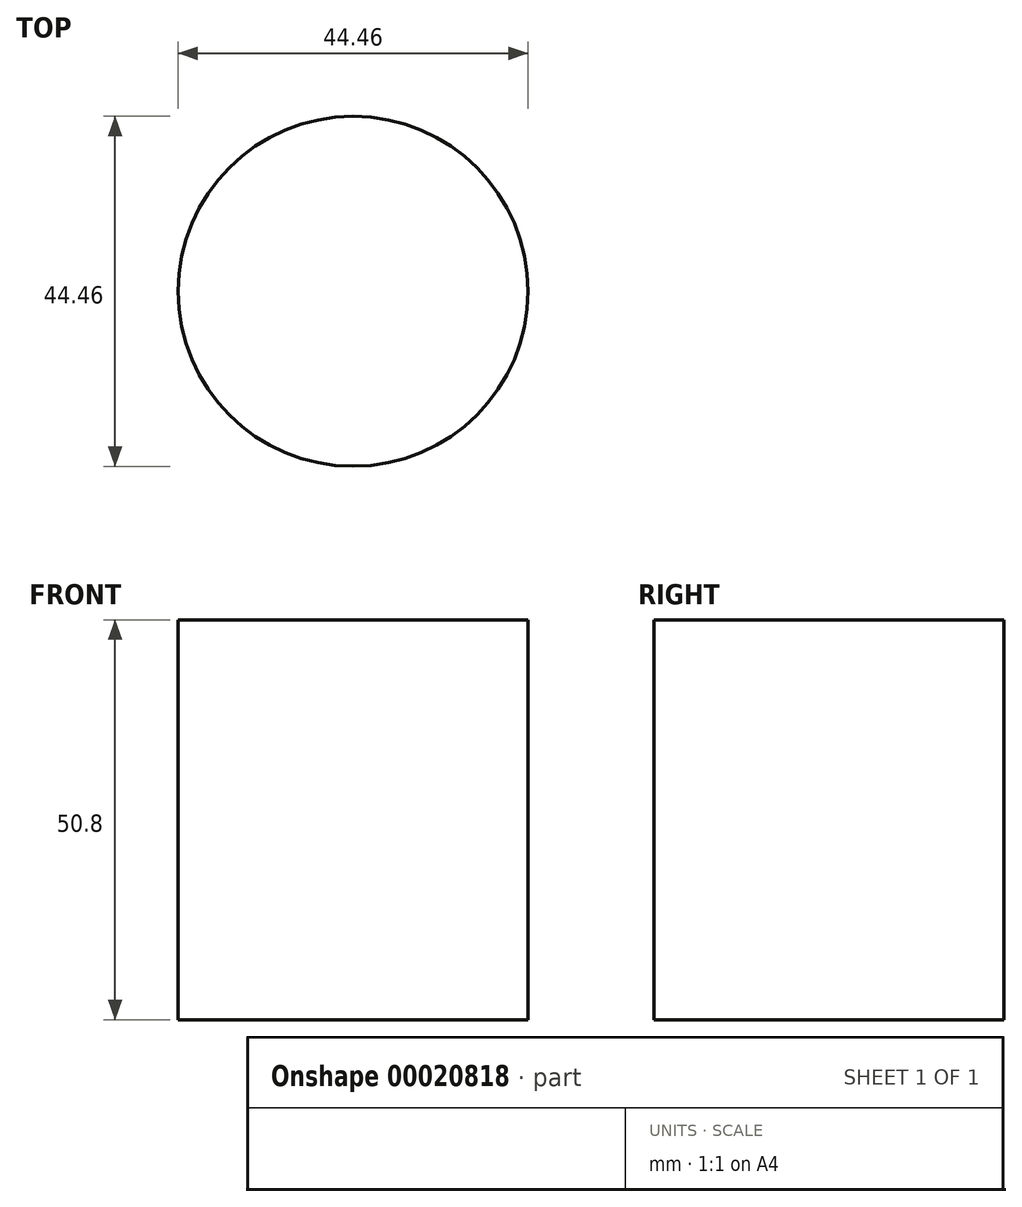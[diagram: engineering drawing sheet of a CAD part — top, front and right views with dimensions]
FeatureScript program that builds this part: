
annotation { "Feature Type Name" : "Feature", "Feature Type Description" : "" }
export const myFeature = defineFeature(function(context is Context, id is Id, definition is map)
    precondition{}
    {
        {
            var Q0;
            Q0=qCreatedBy(makeId("Top.planeOp"),FACE);
            var sketch = newSketch(context, id + "F0", { "sketchPlane" : qUnion([Q0])});
            skCircle(sketch, "E0", {"center": v(0, 0) * mm, "radius": 22.23 * mm});
            skSolve(sketch);
        }
        {
            var Q0;
            Q0 = qSketchRegion(id + "F0", true);
            extrude(context, id + "F1", {"entities" : qUnion([Q0]), "depth" : 50.8 * mm});
        }
    });
